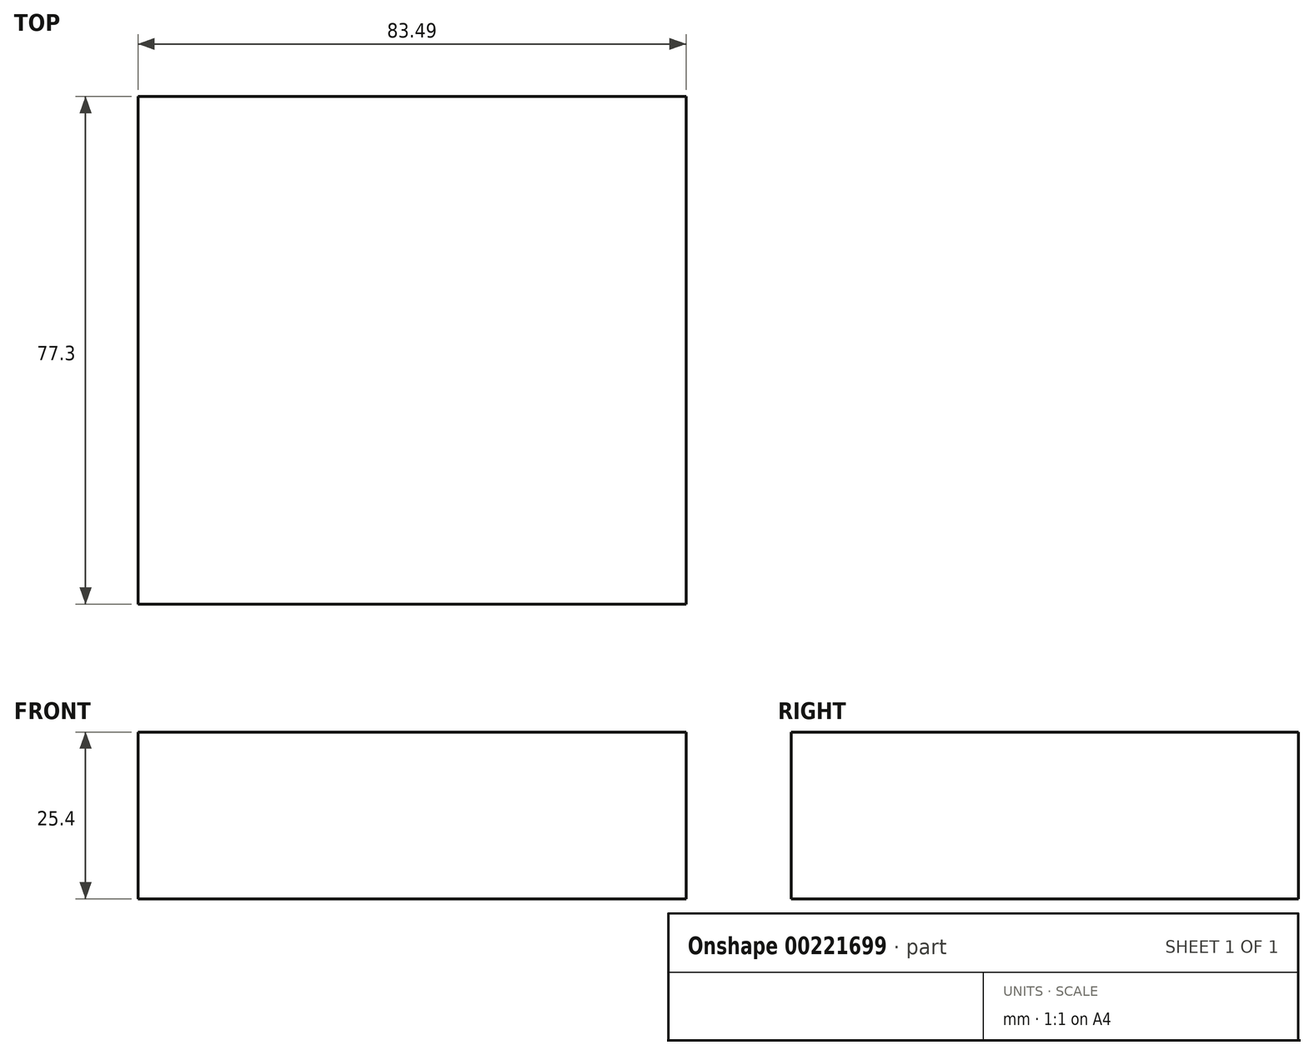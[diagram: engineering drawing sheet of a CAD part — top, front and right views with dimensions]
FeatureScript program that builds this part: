
annotation { "Feature Type Name" : "Feature", "Feature Type Description" : "" }
export const myFeature = defineFeature(function(context is Context, id is Id, definition is map)
    precondition{}
    {
        {
            var Q0;
            Q0=qCreatedBy(makeId("Front.planeOp"),FACE);
            var sketch = newSketch(context, id + "F0", { "sketchPlane" : qUnion([Q0])});
            skCircle(sketch, "E0", {"center": v(0, 0) * mm, "radius": 1.4 * mm});
            skLineSegment(sketch, "E1", {"start": v(0, 10.27) * mm, "end": v(-0.76, 10.27) * mm});
            skLineSegment(sketch, "E2", {"start": v(6.57, -1.14) * mm, "end": v(8.03, -3.22) * mm});
            skLineSegment(sketch, "E3", {"start": v(8.03, -3.22) * mm, "end": v(5.58, -4.37) * mm});
            skLineSegment(sketch, "E4", {"start": v(5.58, -4.37) * mm, "end": v(6.93, -7.25) * mm});
            skPoint(sketch, "E5", {"position": v(8.33, 7.47) * mm});
            skPoint(sketch, "E6", {"position": v(6.4, 3.32) * mm});
            skPoint(sketch, "E7", {"position": v(1.98, 0.63) * mm});
            skPoint(sketch, "E8", {"position": v(-4.2, 11.16) * mm});
            skArc(sketch, "E9", {"start": v(-2.38, 8.11) * mm, "mid": v(-1.34, 9.05) * mm, "end": v(-0.75, 10.32) * mm});
            skArc(sketch, "E10", {"start": v(0, 10.27) * mm, "mid": v(0.71, 3.09) * mm, "end": v(6.57, -1.14) * mm});
            skArc(sketch, "E11", {"start": v(-2.53, -1.18) * mm, "mid": v(-2.34, -1.53) * mm, "end": v(-2.14, -1.87) * mm});
            skLineSegment(sketch, "E12", {"start": v(0, 0) * mm, "end": v(-9.24, -4.33) * mm, "construction": true});
            skLineSegment(sketch, "E13", {"start": v(0, 0) * mm, "end": v(13.07, -27.9) * mm, "construction": true});
            skLineSegment(sketch, "E14", {"start": v(4.93, -8.74) * mm, "end": v(3.79, -6.3) * mm});
            skArc(sketch, "E15", {"start": v(4.93, -8.74) * mm, "mid": v(5.98, -8.06) * mm, "end": v(6.93, -7.25) * mm});
            skArc(sketch, "E16.converted", {"start": v(-2.38, 8.11) * mm, "mid": v(-3.6, 3.09) * mm, "end": v(-2.14, -1.87) * mm});
            skArc(sketch, "E17", {"start": v(3.79, -6.3) * mm, "mid": v(2.66, -4.86) * mm, "end": v(1, -4.1) * mm});
            skArc(sketch, "E18.trimOffspring", {"start": v(-2.5, -1.17) * mm, "mid": v(-0.73, -3.36) * mm, "end": v(1.96, -4.2) * mm});
            skPoint(sketch, "E19", {"position": v(-7.25, -4.3) * mm});
            skArc(sketch, "E20.trimOffspring", {"start": v(-0.45, 7.03) * mm, "mid": v(-1.42, 7.56) * mm, "end": v(-2.43, 8) * mm});
            skArc(sketch, "E21.trimOffspring", {"start": v(5.96, -4.2) * mm, "mid": v(5.84, -2.5) * mm, "end": v(5.5, -0.86) * mm});
            skSolve(sketch);
        }
        {
            var Q0;
            Q0 = qSketchRegion(id + "F0", true);
            extrude(context, id + "F1", {"entities" : qUnion([Q0]), "oppositeDirection" : true, "depth" : ((.309 - .117) / 2) * mm});
        }
        {
            var Q0;
            Q0 = qSketchRegion(id + "F0", true);
            extrude(context, id + "F2", {"entities" : qUnion([Q0]), "oppositeDirection" : true, "depth" : 7.85 * mm, "hasSecondDirection" : true, "secondDirectionOppositeDirection" : true, "secondDirectionDepth" : (((.309 - .117) / 2) + .117) * mm});
        }
        {
            var Q0;
            {var subQ5=sQuery(id+"F0.wireOp",EDGE,"E1");Q0=makeQuery(id+"F0.imprint","IMPRINT",FACE,{"disambiguationData":[TD([[makeQuery(id+"F0.imprint","IMPRINT",EDGE,{"derivedFrom":subQ5}),1.0]])]});}
            var Q1;
            {var subQ0=sQuery(id+"F0.wireOp",EDGE,"E2");Q1=makeQuery(id+"F0.imprint","IMPRINT",FACE,{"disambiguationData":[TD([[makeQuery(id+"F0.imprint","IMPRINT",EDGE,{"derivedFrom":subQ0}),-1.0]])]});}
            extrude(context, id + "F3", {"entities" : qUnion([Q0, Q1]), "operationType" : NewBodyOperationType.ADD, "oppositeDirection" : true, "depth" : 7.85 * mm});
        }
        {
            var Q0;
            Q0=makeQuery(id+"F1.opExtrude","CAP_EDGE",EDGE,{"disambiguationData":[OSD([sQuery(id+"F0.wireOp",EDGE,"E0")])],"isStart":true});
            chamfer(context, id + "F4", {"entities" : qUnion([Q0]), "chamferType" : ChamferType.OFFSET_ANGLE, "width" : 0.38 * mm, "oppositeDirection" : false, "angle" : 30 * degree, "tangentPropagation" : true});
        }
        {
            var Q0;
            Q0=makeQuery(id+"F2.opExtrude","CAP_EDGE",EDGE,{"disambiguationData":[OSD([sQuery(id+"F0.wireOp",EDGE,"E0")])],"isStart":false});
            chamfer(context, id + "F5", {"entities" : qUnion([Q0]), "chamferType" : ChamferType.OFFSET_ANGLE, "width" : 0.38 * mm, "oppositeDirection" : true, "angle" : 30 * degree, "tangentPropagation" : true});
        }
        {
            var Q0;
            {var subQ0=sQuery(id+"F0.wireOp",EDGE,"E3");Q0=makeQuery(id+"F3.boolean.opBoolean","MERGE",FACE,{"derivedFrom":[makeQuery(id+"F1.opExtrude","SWEPT_FACE",FACE,{"disambiguationData":[OSD([subQ0])]}),makeQuery(id+"F2.opExtrude","SWEPT_FACE",FACE,{"disambiguationData":[OSD([subQ0])]}),makeQuery(id+"F3.opExtrude","SWEPT_FACE",FACE,{"disambiguationData":[OSD([subQ0])]})]});}
            var Q1;
            Q1=makeQuery(id+"F1.opExtrude","CAP_VERTEX",VERTEX,{"disambiguationData":[OSD([sQuery(id+"F0.wireOp",EDGE,"E14"),sQuery(id+"F0.wireOp",EDGE,"E15")])],"isStart":false});
            cPlane(context, id + "F6", {"entities" : qUnion([Q0, Q1]), "cplaneType" : CPlaneType.PLANE_POINT, "offset" : 25.4 * mm, "width" : 152.4 * mm, "height" : 152.4 * mm});
        }
        {
            var Q0;
            Q0=qCreatedBy(id+"F6.planeOp",FACE);
            var sketch = newSketch(context, id + "F7", { "sketchPlane" : qUnion([Q0])});
            skLineSegment(sketch, "E22", {"start": v(-3.3, 2.15) * mm, "end": v(1.27, -2.43) * mm});
            skLineSegment(sketch, "E23", {"start": v(1.27, -5.41) * mm, "end": v(-0.62, -7.3) * mm});
            skLineSegment(sketch, "E24", {"start": v(3.62, -2.44) * mm, "end": v(3.62, -5.41) * mm});
            skLineSegment(sketch, "E25", {"start": v(3.62, -3.92) * mm, "end": v(3.62, -3.92) * mm});
            skPoint(sketch, "E25.endSnap0", {"position": v(3.62, -3.92) * mm});
            skLineSegment(sketch, "E26", {"start": v(1.27, -7.41) * mm, "end": v(1.27, 1.31) * mm});
            skLineSegment(sketch, "E27", {"start": v(-0.79, -2.44) * mm, "end": v(1.27, -2.43) * mm});
            skLineSegment(sketch, "E28", {"start": v(1.27, -5.41) * mm, "end": v(-1.06, -5.41) * mm});
            skLineSegment(sketch, "E29", {"start": v(0.76, 1.1) * mm, "end": v(0.76, -7.1) * mm});
            skSolve(sketch);
        }
        {
            var Q0;
            {var subQ1=sQuery(id+"F7.wireOp",EDGE,"E22");var subQ3=sQuery(id+"F7.wireOp",EDGE,"E29");var subQ4=makeQuery(id+"F7.imprint","INTERSECT",VERTEX,{"derivedFrom":[subQ1,subQ3]});Q0=makeQuery(id+"F7.imprint","IMPRINT",FACE,{"disambiguationData":[TD([[makeQuery(id+"F7.imprint","IMPRINT",EDGE,{"disambiguationData":[TD([[subQ4,-1.0]])],"derivedFrom":subQ3}),1.0]])]});}
            var Q1;
            {var subQ1=sQuery(id+"F7.wireOp",EDGE,"E23");var subQ3=sQuery(id+"F7.wireOp",EDGE,"E29");var subQ4=makeQuery(id+"F7.imprint","INTERSECT",VERTEX,{"derivedFrom":[subQ1,subQ3]});Q1=makeQuery(id+"F7.imprint","IMPRINT",FACE,{"disambiguationData":[TD([[makeQuery(id+"F7.imprint","IMPRINT",EDGE,{"disambiguationData":[TD([[subQ4,1.0]])],"derivedFrom":subQ3}),1.0]])]});}
            extrude(context, id + "F8", {"entities" : qUnion([Q0, Q1]), "operationType" : NewBodyOperationType.REMOVE, "oppositeDirection" : true, "depth" : 1.78 * mm});
        }
        {
            var Q0;
            Q0=makeQuery(id+"F8.boolean.opBoolean","COPY",EDGE,{"derivedFrom":makeQuery(id+"F8.opExtrude","CAP_EDGE",EDGE,{"disambiguationData":[OSD([sQuery(id+"F7.wireOp",EDGE,"E23")])],"isStart":false})});
            var Q1;
            Q1=makeQuery(id+"F8.boolean.opBoolean","COPY",EDGE,{"derivedFrom":makeQuery(id+"F8.opExtrude","CAP_EDGE",EDGE,{"disambiguationData":[OSD([sQuery(id+"F7.wireOp",EDGE,"E22")])],"isStart":false})});
            fillet(context, id + "F9", {"entities" : qUnion([Q0, Q1]), "radius" : 0.13 * mm, "tangentPropagation" : true, "allowEdgeOverflow" : false});
        }
        {
            var Q0;
            Q0=makeQuery(id+"F0.imprint","IMPRINT",FACE,{"disambiguationData":[TD([[makeQuery(id+"F0.imprint","IMPRINT",EDGE,{"derivedFrom":sQuery(id+"F0.wireOp",EDGE,"E0")}),-1.0]])]});
            var sketch = newSketch(context, id + "F10", { "sketchPlane" : qUnion([Q0])});
            skCircle(sketch, "E30", {"center": v(0, 0) * mm, "radius": 1.6 * mm});
            skSolve(sketch);
        }
        {
            var Q0;
            Q0 = qSketchRegion(id + "F10", true);
            extrude(context, id + "F11", {"entities" : qUnion([Q0]), "operationType" : NewBodyOperationType.ADD, "oppositeDirection" : true, "depth" : ((.309 - .117) / 2 - .5) * mm, "hasSecondDirection" : true, "secondDirectionOppositeDirection" : true, "secondDirectionDepth" : 0.18 * mm});
        }
        {
            var Q0;
            Q0=makeQuery(id+"F2.opExtrude","CAP_FACE",FACE,{"disambiguationData":[OSD([sQuery(id+"F0.wireOp",EDGE,"E0"),sQuery(id+"F0.wireOp",EDGE,"E1"),sQuery(id+"F0.wireOp",EDGE,"E2"),sQuery(id+"F0.wireOp",EDGE,"E3"),sQuery(id+"F0.wireOp",EDGE,"E4"),sQuery(id+"F0.wireOp",EDGE,"E9"),sQuery(id+"F0.wireOp",EDGE,"E10"),sQuery(id+"F0.wireOp",EDGE,"E14"),sQuery(id+"F0.wireOp",EDGE,"E15"),sQuery(id+"F0.wireOp",EDGE,"E16.converted"),sQuery(id+"F0.wireOp",EDGE,"E17"),sQuery(id+"F0.wireOp",EDGE,"E18.trimOffspring")])],"isStart":false});
            var sketch = newSketch(context, id + "F12", { "sketchPlane" : qUnion([Q0])});
            skCircle(sketch, "E31", {"center": v(0, 0) * mm, "radius": 1.52 * mm});
            skSolve(sketch);
        }
        {
            var Q0;
            Q0 = qSketchRegion(id + "F12", true);
            extrude(context, id + "F13", {"entities" : qUnion([Q0]), "operationType" : NewBodyOperationType.ADD, "oppositeDirection" : true, "depth" : 2.31 * mm, "hasSecondDirection" : true, "secondDirectionOppositeDirection" : true, "secondDirectionDepth" : 0.18 * mm});
        }
        {
            var Q0;
            Q0=qCreatedBy(makeId("Top.planeOp"),FACE);
            var sketch = newSketch(context, id + "F14", { "sketchPlane" : qUnion([Q0])});
            skLineSegment(sketch, "E32.bottom", {"start": v(-38.62, 36.4) * mm, "end": v(44.87, 36.4) * mm});
            skLineSegment(sketch, "E32.top", {"start": v(-38.62, -40.9) * mm, "end": v(44.87, -40.9) * mm});
            skLineSegment(sketch, "E32.left", {"start": v(-38.62, 36.4) * mm, "end": v(-38.62, -40.9) * mm});
            skLineSegment(sketch, "E32.right", {"start": v(44.87, 36.4) * mm, "end": v(44.87, -40.9) * mm});
            skSolve(sketch);
        }
        {
            var Q0;
            Q0 = qSketchRegion(id + "F14", true);
            extrude(context, id + "F15", {"entities" : qUnion([Q0]), "operationType" : NewBodyOperationType.ADD, "endBound" : BoundingType.SYMMETRIC, "depth" : 25.4 * mm});
        }
    });
